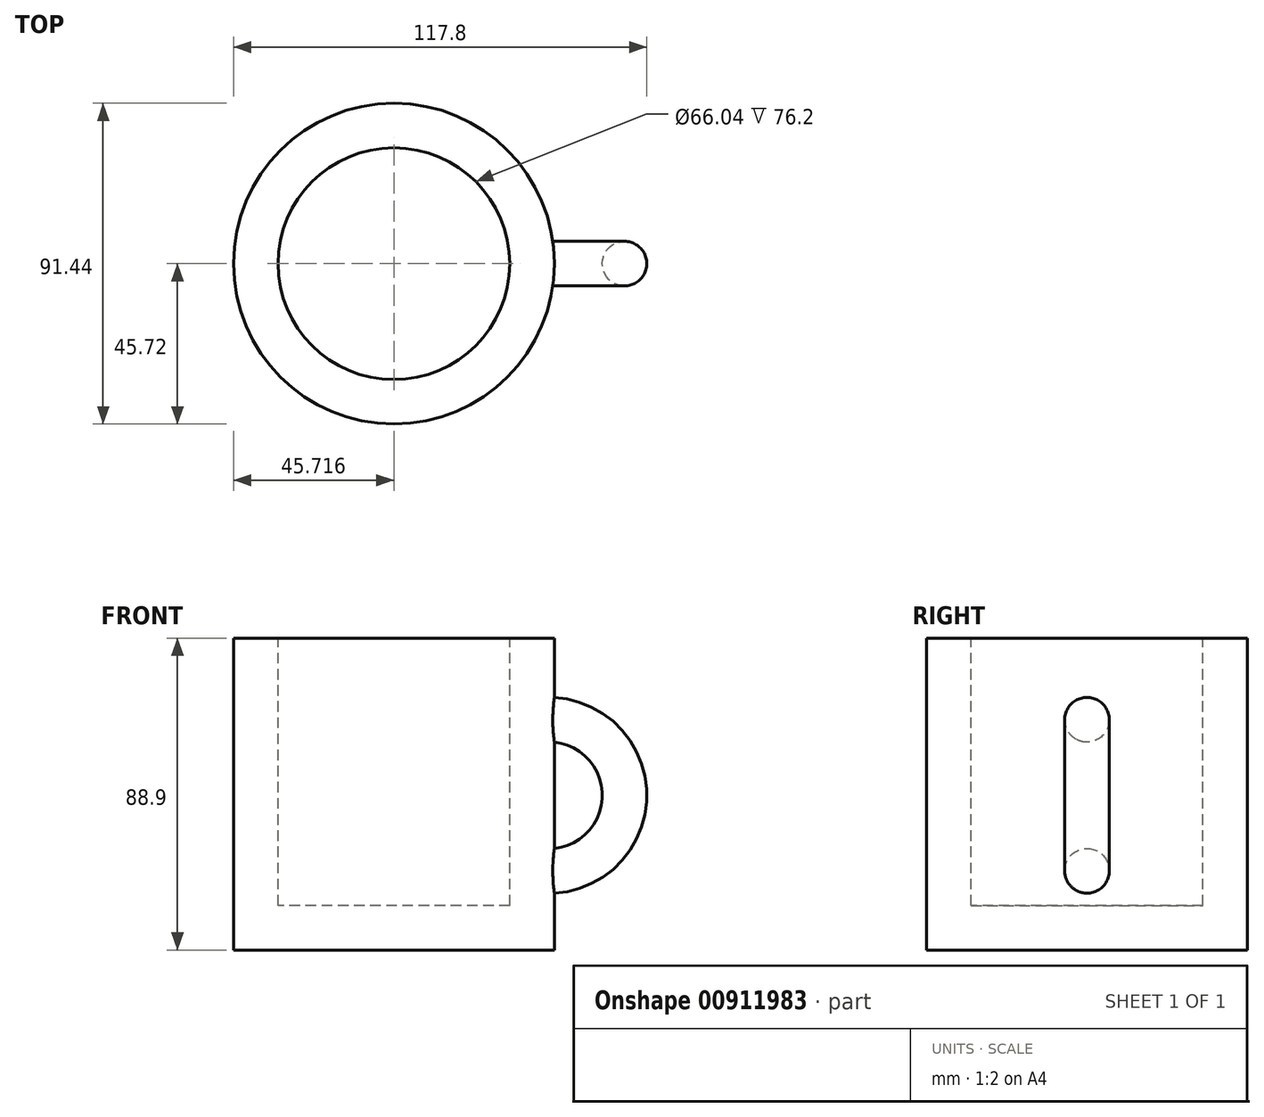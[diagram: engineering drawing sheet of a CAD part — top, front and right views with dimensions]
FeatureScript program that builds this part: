
annotation { "Feature Type Name" : "Feature", "Feature Type Description" : "" }
export const myFeature = defineFeature(function(context is Context, id is Id, definition is map)
    precondition{}
    {
        {
            var Q0;
            Q0=qCreatedBy(makeId("Front.planeOp"),FACE);
            var sketch = newSketch(context, id + "F0", { "sketchPlane" : qUnion([Q0])});
            skLineSegment(sketch, "E0.bottom", {"start": v(1.57, 88.9) * mm, "end": v(-11.13, 88.9) * mm});
            skLineSegment(sketch, "E0.top", {"start": v(1.57, 12.7) * mm, "end": v(-11.13, 12.7) * mm});
            skLineSegment(sketch, "E0.left", {"start": v(1.57, 88.9) * mm, "end": v(1.57, 12.7) * mm});
            skLineSegment(sketch, "E0.right", {"start": v(-11.13, 88.9) * mm, "end": v(-11.13, 12.7) * mm});
            skLineSegment(sketch, "E1", {"start": v(-11.13, 88.9) * mm, "end": v(-44.15, 88.9) * mm, "construction": true});
            skLineSegment(sketch, "E2.bottom", {"start": v(1.57, 12.7) * mm, "end": v(-44.15, 12.7) * mm});
            skLineSegment(sketch, "E2.top", {"start": v(1.57, 0) * mm, "end": v(-44.15, 0) * mm});
            skLineSegment(sketch, "E2.left", {"start": v(1.57, 12.7) * mm, "end": v(1.57, 0) * mm});
            skLineSegment(sketch, "E2.right", {"start": v(-44.15, 12.7) * mm, "end": v(-44.15, 0) * mm});
            skLineSegment(sketch, "E3", {"start": v(-44.15, 88.9) * mm, "end": v(-44.15, 12.7) * mm, "construction": true});
            skSolve(sketch);
        }
        {
            var Q0;
            {var subQ0=makeQuery(id+"F0.imprint","IMPRINT",EDGE,{"derivedFrom":sQuery(id+"F0.wireOp",EDGE,"E0.top")});Q0=qUnion([makeQuery(id+"F0.imprint","IMPRINT",FACE,{"disambiguationData":[TD([[makeQuery(id+"F0.imprint","IMPRINT",EDGE,{"derivedFrom":sQuery(id+"F0.wireOp",EDGE,"E0.bottom")}),1.0]])]}),makeQuery(id+"F0.imprint","IMPRINT",FACE,{"disambiguationData":[TD([[subQ0,1.0]])]})]);}
            var Q1;
            Q1=sQuery(id+"F0.wireOp",EDGE,"E3");
            revolve(context, id + "F1", {"surfaceOperationType" : NewSurfaceOperationType.NEW, "entities" : qUnion([Q0]), "axis" : qUnion([Q1]), "revolveType" : RevolveType.FULL});
        }
        {
            var Q0;
            Q0=qCreatedBy(makeId("Right.planeOp"),FACE);
            var sketch = newSketch(context, id + "F2", { "sketchPlane" : qUnion([Q0])});
            skCircle(sketch, "E4", {"center": v(0, 22.5) * mm, "radius": 6.35 * mm});
            skLineSegment(sketch, "E5", {"start": v(0, 44.1) * mm, "end": v(-7.93, 44.1) * mm, "construction": true});
            skLineSegment(sketch, "E6", {"start": v(-7.93, 44.1) * mm, "end": v(7.72, 44.1) * mm, "construction": true});
            skSolve(sketch);
        }
        {
            var Q0;
            Q0 = qSketchRegion(id + "F2", true);
            var Q1;
            Q1=sQuery(id+"F2.wireOp",EDGE,"E6");
            revolve(context, id + "F3", {"operationType" : NewBodyOperationType.ADD, "surfaceOperationType" : NewSurfaceOperationType.NEW, "entities" : qUnion([Q0]), "axis" : qUnion([Q1]), "revolveType" : RevolveType.ONE_DIRECTION, "oppositeDirection" : true, "angle" : 180 * degree});
        }
    });
